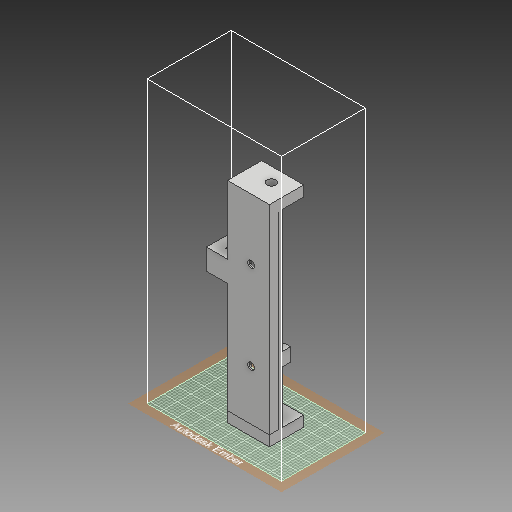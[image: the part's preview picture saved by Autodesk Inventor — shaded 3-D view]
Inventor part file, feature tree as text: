
AUTODESK INVENTOR PART (.ipt)
format: ipt  version: 2018 (Build 220112000, 112)  size: 633,344 bytes
history: native  units: mm
features: sketch x43, extrude x30, hole x8, fillet x5
ambient origin geometry x8: Origin, YZ Plane, XZ Plane, XY Plane, X Axis, Y Axis, Z Axis, Center Point
bodies: Solid1 (feature_tree)
feature tree (86):
  extrude  "Extrusion1"  Depth=100.0mm
  extrude  "Extrusion2"  Depth=5.0mm
  sketch  "Sketch3"  dims[d5=5.0mm d6=40.0mm d7=0.0mm]
  hole  "Hole1"  [1 undecoded]
  extrude  "Extrusion3"  Depth=2.0mm
  hole  "Hole2"  [1 undecoded]
  fillet  "Fillet1"  Radius=8.5mm
  extrude  "Extrusion4"  TaperAngle=90.0deg  [1 undecoded]
  extrude  "Extrusion5"  TaperAngle=180.0deg  [1 undecoded]
  hole  "Hole3"  [1 undecoded]
  fillet  "Fillet2"  Radius=3.5mm
  extrude  "Extrusion6"  Depth=10.0mm
  extrude  "Extrusion7"  Depth=5.0mm TaperAngle=0.0deg
  extrude  "Extrusion8"  Depth=5.0mm TaperAngle=0.0deg
  extrude  "Extrusion9"  Depth=0.1mm
  hole  "Hole4"  [1 undecoded]
  extrude  "Extrusion10"  Depth=5.5mm
  hole  "Hole5"  [1 undecoded]
  extrude  "Extrusion11"  Depth=2.1mm TaperAngle=0.0deg
  extrude  "Extrusion12"  Depth=5.0mm
  extrude  "Extrusion13"  Depth=1.0mm TaperAngle=0.0deg
  extrude  "Extrusion14"  Depth=3.8mm TaperAngle=0.0deg
  sketch  "Sketch21"  dims[d66=6.35mm d67=3.8mm d68=0.0mm]
  extrude  "Extrusion15"  Depth=8.0mm TaperAngle=0.0deg
  sketch  "Sketch23"  dims[d78=3.3mm d79=6.0mm d80=4.0mm d81=2.0mm d82=90.0deg d83=80.0mm d84=20.594885mm d85=5.45mm]
  extrude  "Extrusion16"  Depth=2.0mm
  extrude  "Extrusion17"  Depth=10.5mm
  hole  "Hole6"  [1 undecoded]
  fillet  "Fillet3"  Radius=4.5mm
  extrude  "Extrusion18"  Depth=8.0mm TaperAngle=0.0deg
  sketch  "Sketch28"  dims[d100=4.1mm d101=0.0mm d102=5.0mm]
  extrude  "Extrusion19"  Depth=10.0mm
  extrude  "Extrusion20"  Depth=5.0mm
  extrude  "Extrusion21"  Depth=10.0mm TaperAngle=0.0deg
  hole  "Hole7"  [1 undecoded]
  extrude  "Extrusion22"  Depth=21.0mm
  extrude  "Extrusion23"  Depth=7.499983mm TaperAngle=0.0deg
  fillet  "Fillet4"  Radius=50.0mm
  fillet  "Fillet5"  Radius=7.499983mm
  extrude  "Extrusion24"  Depth=10.0mm
  extrude  "Extrusion25"  Depth=4.1mm TaperAngle=0.0deg
  hole  "Hole8"  [1 undecoded]
  extrude  "Extrusion26"  Depth=8.0mm TaperAngle=0.0deg
  sketch  "Sketch39"  dims[d142=3.85mm d143=0.0mm d144=3.0mm]
  extrude  "Extrusion27"  Depth=1.0mm
  extrude  "Extrusion28"  Depth=3.0mm
  extrude  "Extrusion29"  Depth=100.0mm TaperAngle=0.0deg
  extrude  "Extrusion30"  Depth=10.0mm
  sketch  "Sketch1"  dims[d0=22.65mm d1=100.0mm]
  sketch  "Sketch2"  dims[d2=5.0mm d3=0.0mm d4=5.0mm]
  sketch  "Sketch4"  dims[d8=10.0mm]
  sketch  "Sketch5"  dims[d9=4.0mm d10=6.0mm d11=4.0mm d12=2.0mm d13=90.0deg d14=115.0mm d15=20.594885mm d16=23.0mm]
  sketch  "Sketch6"  dims[d17=102.75mm d18=0.0mm d19=1.175mm d20=8.5mm]
  sketch  "Sketch7"  dims[d21=21.0mm d22=90.0deg]
  sketch  "Sketch8"  dims[d23=8.5mm d24=180.0deg]
  sketch  "Sketch9"  dims[d25=21.0mm]
  sketch  "Sketch10"  dims[d26=4.0mm d27=6.0mm d28=4.0mm d29=2.0mm d30=90.0deg d31=115.0mm d32=20.594885mm d33=1.0mm d34=3.5mm]
  sketch  "Sketch11"  dims[d35=15.825mm d36=10.0mm]
  sketch  "Sketch12"  dims[d37=10.0mm d38=5.0mm d39=0.0mm]
  sketch  "Sketch13"  dims[d40=5.0mm d41=12.5mm d42=0.0mm]
  sketch  "Sketch14"  dims[d43=6.0mm d44=6.0mm d45=4.0mm d46=2.0mm d47=90.0deg d48=115.0mm d49=20.594885mm d50=0.1mm]
  sketch  "Sketch15"  dims[d51=4.25mm d52=1000.0mm d53=0.0mm]
  sketch  "Sketch16"  dims[d54=3.3mm d55=5.5mm]
  sketch  "Sketch17"  dims[d56=3.2mm d57=3.0mm]
  sketch  "Sketch18"  dims[d58=2.1mm d59=91.25mm d60=0.0mm]
  sketch  "Sketch19"  dims[d61=4.44mm d62=5.0mm]
  sketch  "Sketch20"  dims[d63=1.0mm d64=91.25mm d65=0.0mm]
  sketch  "Sketch22"  dims[d69=3.3mm d70=6.0mm d71=4.0mm d72=2.0mm d73=90.0deg d74=8.0mm d75=20.594885mm d76=4.55mm d77=0.0mm]
  sketch  "Sketch24"  dims[d86=129.8mm d87=0.0mm d88=10.5mm]
  sketch  "Sketch25"  dims[d89=2.5mm d90=0.0mm d91=10.0mm d92=4.5mm d93=0.0mm]
  sketch  "Sketch26"  dims[d94=8.0mm d95=0.0mm d96=15.5mm d97=0.0mm]
  sketch  "Sketch27"  dims[d98=10.0mm d99=10.0mm]
  sketch  "Sketch29"  dims[d103=17.5mm d104=10.0mm d105=0.0mm]
  sketch  "Sketch30"  dims[d106=5.0mm]
  sketch  "Sketch31"  dims[d107=6.0mm d108=6.0mm d109=4.0mm d110=2.0mm d111=90.0deg d112=80.0mm d113=20.594885mm d114=2.0mm]
  sketch  "Sketch32"  dims[d115=45.0mm d116=0.0mm d117=21.0mm]
  sketch  "Sketch33"  dims[d118=4.5mm d119=118.0mm d120=0.0mm d121=50.0mm d122=7.499983mm]
  sketch  "Sketch34"  dims[d123=7.5mm d124=10.0mm]
  sketch  "Sketch35"  dims[d125=10.0mm d126=4.1mm d127=0.0mm]
  sketch  "Sketch36"  dims[d128=13.4mm d129=0.0mm d130=5.0mm]
  sketch  "Sketch37"  dims[d131=6.0mm d132=6.0mm d133=4.0mm d134=2.0mm d135=90.0deg d136=8.0mm d137=20.594885mm d138=130.4mm d139=0.0mm]
  sketch  "Sketch38"  dims[d140=1.0mm d141=1.0mm]
  sketch  "Sketch40"  dims[d145=2.0mm d146=100.0mm d147=0.0mm]
  sketch  "Sketch41"  dims[d148=4.0mm d149=10.0mm]
  sketch  "Sketch42"  dims[d150=5.0mm]
  sketch  "Sketch43"  dims[d151=15.0mm d152=7.5mm d153=7.5mm d154=0.0mm d155=6.0mm d156=6.0mm d157=4.0mm d158=2.0mm d159=90.0deg d160=8.0mm d161=20.594885mm d162=5.5mm d163=5.0mm d164=0.0mm d165=5.5mm d166=0.0mm d167=2.0mm d168=0.0mm d169=2.0mm d170=0.0mm d171=2.0mm d172=0.0mm]
note: 10 required parameter values undecoded (feature->parameter linkage not recoverable at this tier; creation-order binding heuristic only, values carry confidence <= 0.55)
